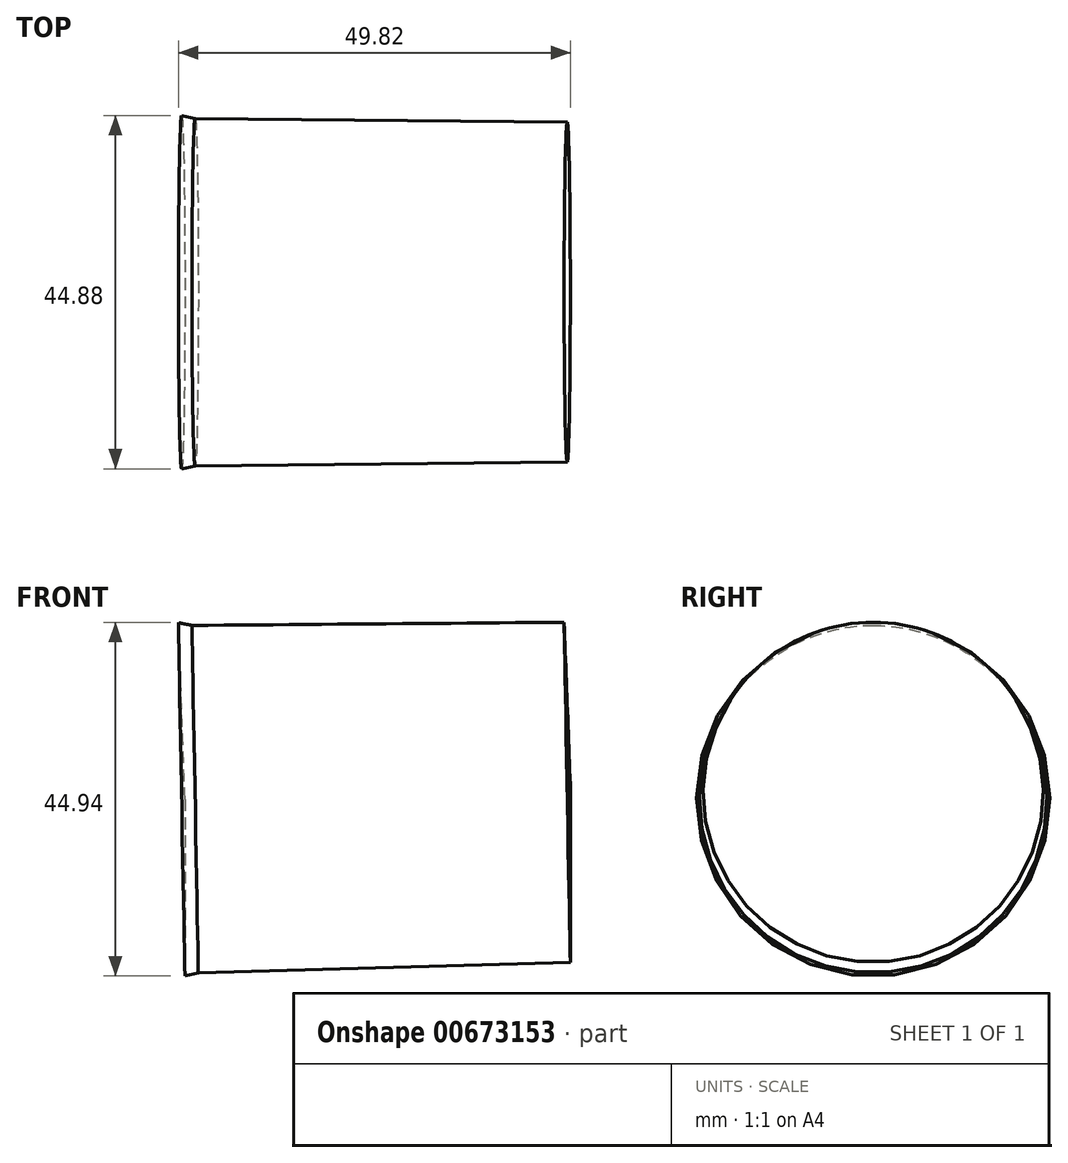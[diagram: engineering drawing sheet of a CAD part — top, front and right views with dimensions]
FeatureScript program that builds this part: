
annotation { "Feature Type Name" : "Feature", "Feature Type Description" : "" }
export const myFeature = defineFeature(function(context is Context, id is Id, definition is map)
    precondition{}
    {
        {
            var Q0;
            Q0=qCreatedBy(makeId("Front.planeOp"),FACE);
            var sketch = newSketch(context, id + "F0", { "sketchPlane" : qUnion([Q0])});
            skLineSegment(sketch, "E0", {"start": v(-38.64, -3.13) * mm, "end": v(-38.64, 19.32) * mm});
            skLineSegment(sketch, "E1", {"start": v(-38.64, 19.32) * mm, "end": v(10.35, 20.22) * mm});
            skLineSegment(sketch, "E2", {"start": v(10.35, 20.22) * mm, "end": v(10.32, -1.38) * mm});
            skLineSegment(sketch, "E3", {"start": v(10.32, -1.38) * mm, "end": v(-36.93, -2.72) * mm});
            skLineSegment(sketch, "E4", {"start": v(-36.93, -2.72) * mm, "end": v(-38.64, -3.13) * mm});
            skSolve(sketch);
        }
        {
            var Q0;
            Q0=makeQuery(id+"F0.imprint","IMPRINT",FACE,{"disambiguationData":[TD([[makeQuery(id+"F0.imprint","IMPRINT",EDGE,{"derivedFrom":sQuery(id+"F0.wireOp",EDGE,"E0")}),-1.0]])]});
            var Q1;
            Q1=sQuery(id+"F0.wireOp",EDGE,"E1");
            revolve(context, id + "F1", {"entities" : qUnion([Q0]), "axis" : qUnion([Q1]), "revolveType" : RevolveType.FULL});
        }
    });
